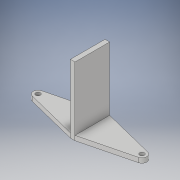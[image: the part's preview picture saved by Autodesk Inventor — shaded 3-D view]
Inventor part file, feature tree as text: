
AUTODESK INVENTOR PART (.ipt)
format: ipt  version: 2019 (Build 230136000, 136)  size: 118,272 bytes
history: native  units: mm
features: extrude x2
ambient origin geometry x8: Origin, YZ Plane, XZ Plane, XY Plane, X Axis, Y Axis, Z Axis, Center Point
bodies: Body1 (feature_tree)
feature tree (2):
  extrude  "Выдавливание2"  Depth=4.0mm
  extrude  "Выдавливание3"  Depth=4.0mm
